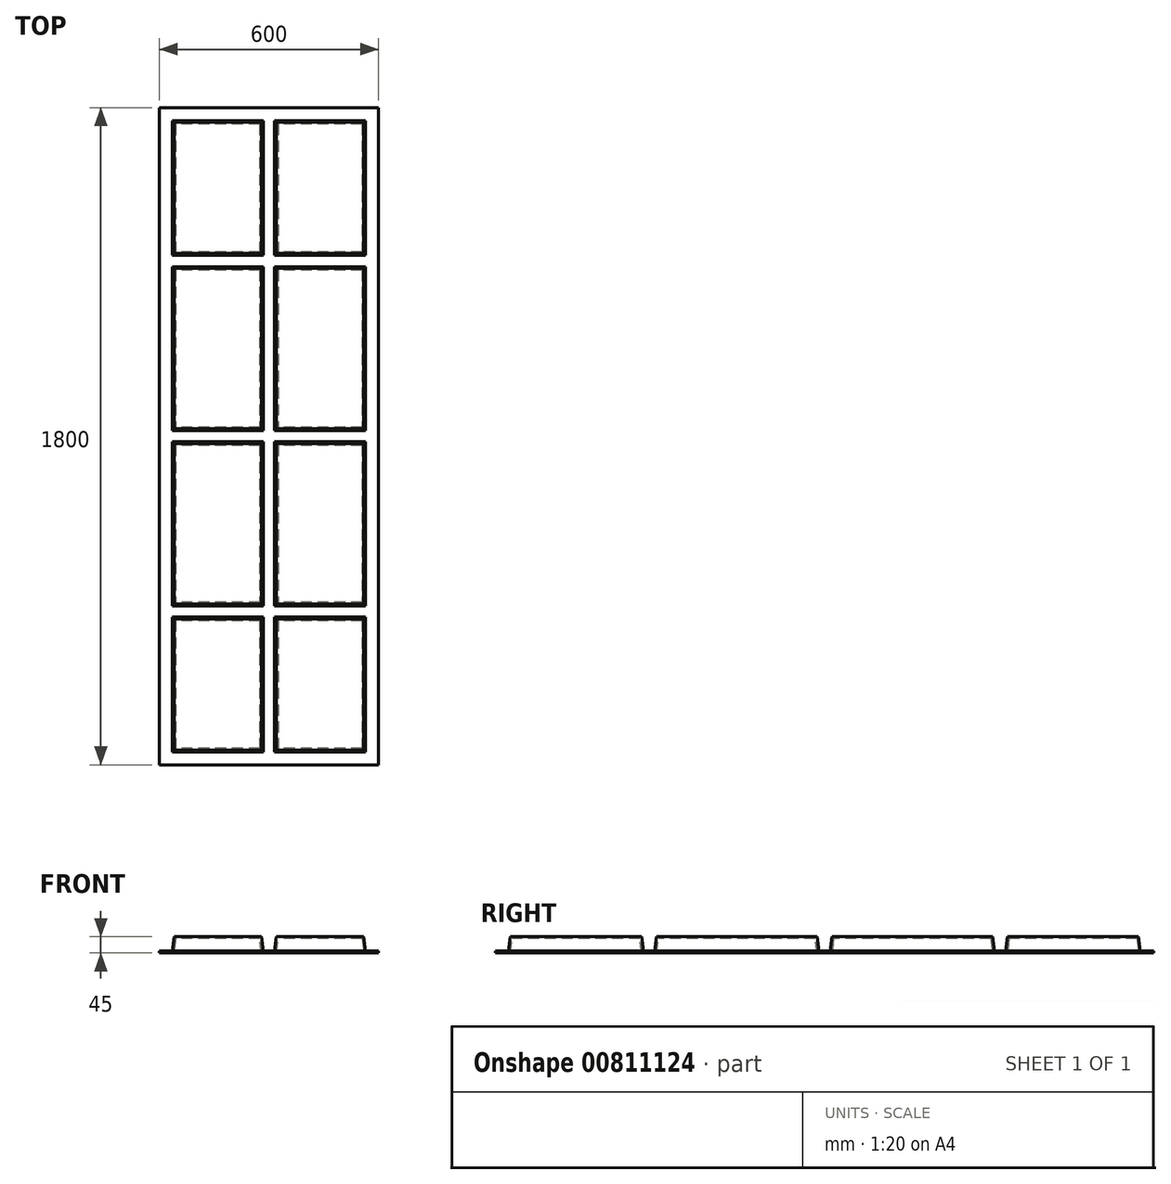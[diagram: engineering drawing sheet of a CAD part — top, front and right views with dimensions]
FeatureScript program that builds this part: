
annotation { "Feature Type Name" : "Feature", "Feature Type Description" : "" }
export const myFeature = defineFeature(function(context is Context, id is Id, definition is map)
    precondition{}
    {
        {
            var Q0;
            Q0=qCreatedBy(makeId("Front.planeOp"),FACE);
            var sketch = newSketch(context, id + "F0", { "sketchPlane" : qUnion([Q0])});
            skLineSegment(sketch, "E0", {"start": v(-170.34, 259.45) * mm, "end": v(-170.34, 254.45) * mm});
            skLineSegment(sketch, "E1.0", {"start": v(129.66, 259.45) * mm, "end": v(129.66, 254.45) * mm});
            skLineSegment(sketch, "E2", {"start": v(-170.34, 254.45) * mm, "end": v(-130.34, 254.45) * mm});
            skLineSegment(sketch, "E3", {"start": v(-125.34, 294.45) * mm, "end": v(104.66, 294.45) * mm});
            skLineSegment(sketch, "E4", {"start": v(109.66, 254.45) * mm, "end": v(129.66, 254.45) * mm});
            skLineSegment(sketch, "E5", {"start": v(-130.34, 254.45) * mm, "end": v(-125.34, 294.45) * mm});
            skLineSegment(sketch, "E6", {"start": v(104.66, 294.45) * mm, "end": v(109.66, 254.45) * mm});
            skLineSegment(sketch, "E7.1", {"start": v(-170.34, 259.45) * mm, "end": v(-134.75, 259.45) * mm});
            skLineSegment(sketch, "E8.1", {"start": v(-134.75, 259.45) * mm, "end": v(-129.75, 299.45) * mm});
            skLineSegment(sketch, "E9.0", {"start": v(114.08, 259.45) * mm, "end": v(129.66, 259.45) * mm});
            skLineSegment(sketch, "E9.1", {"start": v(109.08, 299.45) * mm, "end": v(114.08, 259.45) * mm});
            skLineSegment(sketch, "E9.2", {"start": v(-129.75, 299.45) * mm, "end": v(109.08, 299.45) * mm});
            skLineSegment(sketch, "E10.MirrorCS", {"start": v(149.66, 254.45) * mm, "end": v(129.66, 254.45) * mm});
            skLineSegment(sketch, "E11.MirrorCS", {"start": v(145.25, 259.45) * mm, "end": v(129.66, 259.45) * mm});
            skLineSegment(sketch, "E12.MirrorCS", {"start": v(150.25, 299.45) * mm, "end": v(145.25, 259.45) * mm});
            skLineSegment(sketch, "E13.MirrorCS", {"start": v(154.66, 294.45) * mm, "end": v(149.66, 254.45) * mm});
            skLineSegment(sketch, "E14.MirrorCS", {"start": v(389.08, 299.45) * mm, "end": v(150.25, 299.45) * mm});
            skLineSegment(sketch, "E15.MirrorCS", {"start": v(384.66, 294.45) * mm, "end": v(154.66, 294.45) * mm});
            skLineSegment(sketch, "E16.MirrorCS", {"start": v(394.08, 259.45) * mm, "end": v(389.08, 299.45) * mm});
            skLineSegment(sketch, "E17.MirrorCS", {"start": v(389.66, 254.45) * mm, "end": v(384.66, 294.45) * mm});
            skLineSegment(sketch, "E18.MirrorCS", {"start": v(429.66, 254.45) * mm, "end": v(389.66, 254.45) * mm});
            skLineSegment(sketch, "E19.MirrorCS", {"start": v(429.66, 259.45) * mm, "end": v(429.66, 254.45) * mm});
            skLineSegment(sketch, "E20.MirrorCS", {"start": v(429.66, 259.45) * mm, "end": v(394.08, 259.45) * mm});
            skLineSegment(sketch, "E21", {"start": v(-170.34, 254.45) * mm, "end": v(-170.34, 299.45) * mm});
            skLineSegment(sketch, "E22", {"start": v(-170.34, 299.45) * mm, "end": v(-129.75, 299.45) * mm});
            skLineSegment(sketch, "E23", {"start": v(114.08, 259.45) * mm, "end": v(145.25, 259.45) * mm});
            skLineSegment(sketch, "E24", {"start": v(109.08, 299.45) * mm, "end": v(150.25, 299.45) * mm});
            skLineSegment(sketch, "E25", {"start": v(389.08, 299.45) * mm, "end": v(429.66, 299.45) * mm});
            skLineSegment(sketch, "E26", {"start": v(429.66, 299.45) * mm, "end": v(429.66, 259.45) * mm});
            skSolve(sketch);
        }
        {
            var Q0;
            Q0 = qSketchRegion(id + "F0", true);
            extrude(context, id + "F1", {"entities" : qUnion([Q0]), "oppositeDirection" : true, "depth" : 1800 * mm, "offsetDistance" : 25 * mm});
        }
        {
            var Q0;
            Q0=makeQuery(id+"F1.opExtrude","SWEPT_FACE",FACE,{"disambiguationData":[OSD([sQuery(id+"F0.wireOp",EDGE,"E21")])]});
            var sketch = newSketch(context, id + "F2", { "sketchPlane" : qUnion([Q0])});
            skLineSegment(sketch, "E27", {"start": v(0, 254.45) * mm, "end": v(0, 299.45) * mm});
            skLineSegment(sketch, "E28.0", {"start": v(-900, 254.45) * mm, "end": v(-900, 299.45) * mm});
            skLineSegment(sketch, "E29", {"start": v(-900, 299.45) * mm, "end": v(0, 299.45) * mm});
            skLineSegment(sketch, "E30.0", {"start": v(-880.04, 294.45) * mm, "end": v(-439.96, 294.45) * mm});
            skLineSegment(sketch, "E31", {"start": v(-900, 254.45) * mm, "end": v(0, 254.45) * mm});
            skLineSegment(sketch, "E32.0", {"start": v(-900, 259.45) * mm, "end": v(-884.41, 259.45) * mm});
            skLineSegment(sketch, "E33", {"start": v(-40, 254.45) * mm, "end": v(-45, 294.45) * mm});
            skLineSegment(sketch, "E34", {"start": v(-400, 254.45) * mm, "end": v(-395, 294.45) * mm});
            skLineSegment(sketch, "E35", {"start": v(-440, 254.45) * mm, "end": v(-445, 294.45) * mm});
            skLineSegment(sketch, "E36", {"start": v(-880, 254.45) * mm, "end": v(-875, 294.45) * mm});
            skLineSegment(sketch, "E37.0", {"start": v(-884.41, 259.45) * mm, "end": v(-879.41, 299.45) * mm});
            skLineSegment(sketch, "E38.trimOffspring", {"start": v(-879.37, 259.45) * mm, "end": v(-440.62, 259.45) * mm});
            skLineSegment(sketch, "E39.0", {"start": v(-404.41, 259.45) * mm, "end": v(-399.41, 299.45) * mm});
            skLineSegment(sketch, "E40.0", {"start": v(-435.59, 259.45) * mm, "end": v(-440.59, 299.45) * mm});
            skLineSegment(sketch, "E41.trimOffspring", {"start": v(-400.04, 294.45) * mm, "end": v(-39.96, 294.45) * mm});
            skLineSegment(sketch, "E42.0", {"start": v(-35.59, 259.45) * mm, "end": v(-40.59, 299.45) * mm});
            skLineSegment(sketch, "E43.trimOffspring", {"start": v(-35.59, 259.45) * mm, "end": v(0, 259.45) * mm});
            skLineSegment(sketch, "E44.trimOffspring", {"start": v(-399.38, 259.45) * mm, "end": v(-40.63, 259.45) * mm});
            skLineSegment(sketch, "E45.trimOffspring", {"start": v(-435.59, 259.45) * mm, "end": v(-404.41, 259.45) * mm});
            skLineSegment(sketch, "E46.MirrorCS", {"start": v(-900, 259.45) * mm, "end": v(-915.59, 259.45) * mm});
            skLineSegment(sketch, "E47.MirrorCS", {"start": v(-900, 254.45) * mm, "end": v(-1800, 254.45) * mm});
            skLineSegment(sketch, "E48.MirrorCS", {"start": v(-915.59, 259.45) * mm, "end": v(-920.59, 299.45) * mm});
            skLineSegment(sketch, "E49.MirrorCS", {"start": v(-920, 254.45) * mm, "end": v(-925, 294.45) * mm});
            skLineSegment(sketch, "E50.MirrorCS", {"start": v(-919.96, 294.45) * mm, "end": v(-1360.04, 294.45) * mm});
            skLineSegment(sketch, "E51.MirrorCS", {"start": v(-900, 299.45) * mm, "end": v(-1800, 299.45) * mm});
            skLineSegment(sketch, "E52.MirrorCS", {"start": v(-1364.41, 259.45) * mm, "end": v(-1395.59, 259.45) * mm});
            skLineSegment(sketch, "E53.MirrorCS", {"start": v(-1364.41, 259.45) * mm, "end": v(-1359.41, 299.45) * mm});
            skLineSegment(sketch, "E54.MirrorCS", {"start": v(-1395.59, 259.45) * mm, "end": v(-1400.59, 299.45) * mm});
            skLineSegment(sketch, "E55.MirrorCS", {"start": v(-1360, 254.45) * mm, "end": v(-1355, 294.45) * mm});
            skLineSegment(sketch, "E56.MirrorCS", {"start": v(-1400, 254.45) * mm, "end": v(-1405, 294.45) * mm});
            skLineSegment(sketch, "E57.MirrorCS", {"start": v(-1399.96, 294.45) * mm, "end": v(-1760.04, 294.45) * mm});
            skLineSegment(sketch, "E58.MirrorCS", {"start": v(-1400.63, 259.45) * mm, "end": v(-1759.38, 259.45) * mm});
            skLineSegment(sketch, "E59.MirrorCS", {"start": v(-1764.41, 259.45) * mm, "end": v(-1759.41, 299.45) * mm});
            skLineSegment(sketch, "E60.MirrorCS", {"start": v(-1760, 254.45) * mm, "end": v(-1755, 294.45) * mm});
            skLineSegment(sketch, "E61.MirrorCS", {"start": v(-1764.41, 259.45) * mm, "end": v(-1800, 259.45) * mm});
            skLineSegment(sketch, "E62.MirrorCS", {"start": v(-1800, 254.45) * mm, "end": v(-1800, 299.45) * mm});
            skSolve(sketch);
        }
        {
            var Q0;
            {var subQ0=sQuery(id+"F2.wireOp",EDGE,"E61.MirrorCS");Q0=makeQuery(id+"F2.imprint","IMPRINT",FACE,{"disambiguationData":[TD([[makeQuery(id+"F2.imprint","IMPRINT",EDGE,{"derivedFrom":subQ0}),1.0]])]});}
            extrude(context, id + "F3", {"entities" : qUnion([Q0]), "operationType" : NewBodyOperationType.REMOVE, "oppositeDirection" : true, "depth" : 800 * mm, "offsetDistance" : 25 * mm});
        }
        {
            var Q0;
            {var subQ0=sQuery(id+"F2.wireOp",EDGE,"E61.MirrorCS");Q0=makeQuery(id+"F2.imprint","IMPRINT",FACE,{"disambiguationData":[TD([[makeQuery(id+"F2.imprint","IMPRINT",EDGE,{"derivedFrom":subQ0}),-1.0]])]});}
            extrude(context, id + "F4", {"entities" : qUnion([Q0]), "operationType" : NewBodyOperationType.ADD, "oppositeDirection" : true, "depth" : 600 * mm, "offsetDistance" : 25 * mm});
        }
        {
            var Q0;
            {var subQ0=sQuery(id+"F2.wireOp",EDGE,"E59.MirrorCS");var subQ1=sQuery(id+"F2.wireOp",EDGE,"E57.MirrorCS");var subQ2=makeQuery(id+"F2.imprint","INTERSECT",VERTEX,{"derivedFrom":[subQ1,subQ0]});Q0=makeQuery(id+"F2.imprint","IMPRINT",FACE,{"disambiguationData":[TD([[makeQuery(id+"F2.imprint","IMPRINT",EDGE,{"disambiguationData":[TD([[subQ2,1.0]])],"derivedFrom":subQ1}),1.0]])]});}
            extrude(context, id + "F5", {"entities" : qUnion([Q0]), "operationType" : NewBodyOperationType.ADD, "oppositeDirection" : true, "depth" : 600 * mm, "offsetDistance" : 25 * mm});
        }
        {
            var Q0;
            {var subQ1=sQuery(id+"F2.wireOp",EDGE,"E52.MirrorCS");Q0=makeQuery(id+"F2.imprint","IMPRINT",FACE,{"disambiguationData":[TD([[makeQuery(id+"F2.imprint","IMPRINT",EDGE,{"derivedFrom":subQ1}),1.0]])]});}
            var Q1;
            {var subQ2=sQuery(id+"F2.wireOp",EDGE,"E32.0");Q1=makeQuery(id+"F2.imprint","IMPRINT",FACE,{"disambiguationData":[TD([[makeQuery(id+"F2.imprint","IMPRINT",EDGE,{"derivedFrom":subQ2}),1.0]])]});}
            var Q2;
            {var subQ1=sQuery(id+"F2.wireOp",EDGE,"E46.MirrorCS");Q2=makeQuery(id+"F2.imprint","IMPRINT",FACE,{"disambiguationData":[TD([[makeQuery(id+"F2.imprint","IMPRINT",EDGE,{"derivedFrom":subQ1}),1.0]])]});}
            var Q3;
            {var subQ4=sQuery(id+"F2.wireOp",EDGE,"E45.trimOffspring");Q3=makeQuery(id+"F2.imprint","IMPRINT",FACE,{"disambiguationData":[TD([[makeQuery(id+"F2.imprint","IMPRINT",EDGE,{"derivedFrom":subQ4}),1.0]])]});}
            var Q4;
            {var subQ6=sQuery(id+"F2.wireOp",EDGE,"E43.trimOffspring");Q4=makeQuery(id+"F2.imprint","IMPRINT",FACE,{"disambiguationData":[TD([[makeQuery(id+"F2.imprint","IMPRINT",EDGE,{"derivedFrom":subQ6}),1.0]])]});}
            extrude(context, id + "F6", {"entities" : qUnion([Q0, Q1, Q2, Q3, Q4]), "operationType" : NewBodyOperationType.REMOVE, "oppositeDirection" : true, "depth" : 800 * mm, "offsetDistance" : 25 * mm});
        }
        {
            var Q0;
            {var subQ0=sQuery(id+"F2.wireOp",EDGE,"E41.trimOffspring");var subQ1=sQuery(id+"F2.wireOp",EDGE,"E33");var subQ2=makeQuery(id+"F2.imprint","INTERSECT",VERTEX,{"derivedFrom":[subQ1,subQ0]});Q0=makeQuery(id+"F2.imprint","IMPRINT",FACE,{"disambiguationData":[TD([[makeQuery(id+"F2.imprint","IMPRINT",EDGE,{"disambiguationData":[TD([[subQ2,-1.0]])],"derivedFrom":subQ0}),-1.0]])]});}
            var Q1;
            {var subQ0=sQuery(id+"F2.wireOp",EDGE,"E43.trimOffspring");Q1=makeQuery(id+"F2.imprint","IMPRINT",FACE,{"disambiguationData":[TD([[makeQuery(id+"F2.imprint","IMPRINT",EDGE,{"derivedFrom":subQ0}),-1.0]])]});}
            var Q2;
            {var subQ0=sQuery(id+"F2.wireOp",EDGE,"E40.0");var subQ1=sQuery(id+"F2.wireOp",EDGE,"E30.0");var subQ2=makeQuery(id+"F2.imprint","INTERSECT",VERTEX,{"derivedFrom":[subQ1,subQ0]});Q2=makeQuery(id+"F2.imprint","IMPRINT",FACE,{"disambiguationData":[TD([[makeQuery(id+"F2.imprint","IMPRINT",EDGE,{"disambiguationData":[TD([[subQ2,1.0]])],"derivedFrom":subQ1}),-1.0]])]});}
            var Q3;
            {var subQ5=sQuery(id+"F2.wireOp",EDGE,"E45.trimOffspring");Q3=makeQuery(id+"F2.imprint","IMPRINT",FACE,{"disambiguationData":[TD([[makeQuery(id+"F2.imprint","IMPRINT",EDGE,{"derivedFrom":subQ5}),-1.0]])]});}
            var Q4;
            {var subQ0=sQuery(id+"F2.wireOp",EDGE,"E41.trimOffspring");var subQ1=sQuery(id+"F2.wireOp",EDGE,"E34");var subQ2=makeQuery(id+"F2.imprint","INTERSECT",VERTEX,{"derivedFrom":[subQ1,subQ0]});Q4=makeQuery(id+"F2.imprint","IMPRINT",FACE,{"disambiguationData":[TD([[makeQuery(id+"F2.imprint","IMPRINT",EDGE,{"disambiguationData":[TD([[subQ2,1.0]])],"derivedFrom":subQ0}),-1.0]])]});}
            var Q5;
            {var subQ3=sQuery(id+"F2.wireOp",EDGE,"E50.MirrorCS");var subQ5=sQuery(id+"F2.wireOp",EDGE,"E49.MirrorCS");var subQ6=makeQuery(id+"F2.imprint","INTERSECT",VERTEX,{"derivedFrom":[subQ5,subQ3]});Q5=makeQuery(id+"F2.imprint","IMPRINT",FACE,{"disambiguationData":[TD([[makeQuery(id+"F2.imprint","IMPRINT",EDGE,{"disambiguationData":[TD([[subQ6,1.0]])],"derivedFrom":subQ3}),1.0]])]});}
            var Q6;
            {var subQ7=sQuery(id+"F2.wireOp",EDGE,"E46.MirrorCS");Q6=makeQuery(id+"F2.imprint","IMPRINT",FACE,{"disambiguationData":[TD([[makeQuery(id+"F2.imprint","IMPRINT",EDGE,{"derivedFrom":subQ7}),-1.0]])]});}
            var Q7;
            {var subQ7=sQuery(id+"F2.wireOp",EDGE,"E32.0");Q7=makeQuery(id+"F2.imprint","IMPRINT",FACE,{"disambiguationData":[TD([[makeQuery(id+"F2.imprint","IMPRINT",EDGE,{"derivedFrom":subQ7}),-1.0]])]});}
            var Q8;
            {var subQ0=sQuery(id+"F2.wireOp",EDGE,"E37.0");var subQ1=sQuery(id+"F2.wireOp",EDGE,"E30.0");var subQ2=makeQuery(id+"F2.imprint","INTERSECT",VERTEX,{"derivedFrom":[subQ1,subQ0]});Q8=makeQuery(id+"F2.imprint","IMPRINT",FACE,{"disambiguationData":[TD([[makeQuery(id+"F2.imprint","IMPRINT",EDGE,{"disambiguationData":[TD([[subQ2,-1.0]])],"derivedFrom":subQ1}),-1.0]])]});}
            var Q9;
            {var subQ3=sQuery(id+"F2.wireOp",EDGE,"E57.MirrorCS");var subQ5=sQuery(id+"F2.wireOp",EDGE,"E56.MirrorCS");var subQ6=makeQuery(id+"F2.imprint","INTERSECT",VERTEX,{"derivedFrom":[subQ5,subQ3]});Q9=makeQuery(id+"F2.imprint","IMPRINT",FACE,{"disambiguationData":[TD([[makeQuery(id+"F2.imprint","IMPRINT",EDGE,{"disambiguationData":[TD([[subQ6,1.0]])],"derivedFrom":subQ3}),1.0]])]});}
            var Q10;
            {var subQ5=sQuery(id+"F2.wireOp",EDGE,"E52.MirrorCS");Q10=makeQuery(id+"F2.imprint","IMPRINT",FACE,{"disambiguationData":[TD([[makeQuery(id+"F2.imprint","IMPRINT",EDGE,{"derivedFrom":subQ5}),-1.0]])]});}
            var Q11;
            {var subQ0=sQuery(id+"F2.wireOp",EDGE,"E53.MirrorCS");var subQ1=sQuery(id+"F2.wireOp",EDGE,"E50.MirrorCS");var subQ2=makeQuery(id+"F2.imprint","INTERSECT",VERTEX,{"derivedFrom":[subQ1,subQ0]});Q11=makeQuery(id+"F2.imprint","IMPRINT",FACE,{"disambiguationData":[TD([[makeQuery(id+"F2.imprint","IMPRINT",EDGE,{"disambiguationData":[TD([[subQ2,1.0]])],"derivedFrom":subQ1}),1.0]])]});}
            extrude(context, id + "F7", {"entities" : qUnion([Q0, Q1, Q2, Q3, Q4, Q5, Q6, Q7, Q8, Q9, Q10, Q11]), "operationType" : NewBodyOperationType.ADD, "oppositeDirection" : true, "depth" : 600 * mm, "offsetDistance" : 25 * mm});
        }
        {
            var Q0;
            {var subQ0=sQuery(id+"F0.wireOp",EDGE,"E7.1");Q0=makeQuery(id+"F0.imprint","IMPRINT",FACE,{"disambiguationData":[TD([[makeQuery(id+"F0.imprint","IMPRINT",EDGE,{"derivedFrom":subQ0}),1.0]])]});}
            extrude(context, id + "F8", {"entities" : qUnion([Q0]), "operationType" : NewBodyOperationType.REMOVE, "oppositeDirection" : true, "depth" : 1900 * mm, "offsetDistance" : 25 * mm});
        }
        {
            var Q0;
            {var subQ3=sQuery(id+"F0.wireOp",EDGE,"E9.1");Q0=makeQuery(id+"F0.imprint","IMPRINT",FACE,{"disambiguationData":[TD([[makeQuery(id+"F0.imprint","IMPRINT",EDGE,{"derivedFrom":subQ3}),1.0]])]});}
            extrude(context, id + "F9", {"entities" : qUnion([Q0]), "operationType" : NewBodyOperationType.REMOVE, "oppositeDirection" : true, "depth" : 1900 * mm, "offsetDistance" : 25 * mm});
        }
        {
            var Q0;
            Q0=makeQuery(id+"F0.imprint","IMPRINT",FACE,{"disambiguationData":[TD([[makeQuery(id+"F0.imprint","IMPRINT",EDGE,{"derivedFrom":sQuery(id+"F0.wireOp",EDGE,"E16.MirrorCS")}),-1.0]])]});
            extrude(context, id + "F10", {"entities" : qUnion([Q0]), "operationType" : NewBodyOperationType.REMOVE, "oppositeDirection" : true, "depth" : 1900 * mm, "offsetDistance" : 25 * mm});
        }
        {
            var Q0;
            {var subQ4=sQuery(id+"F2.wireOp",EDGE,"E61.MirrorCS");Q0=makeQuery(id+"F2.imprint","IMPRINT",FACE,{"disambiguationData":[TD([[makeQuery(id+"F2.imprint","IMPRINT",EDGE,{"derivedFrom":subQ4}),-1.0]])]});}
            var Q1;
            {var subQ1=sQuery(id+"F2.wireOp",EDGE,"E52.MirrorCS");Q1=makeQuery(id+"F2.imprint","IMPRINT",FACE,{"disambiguationData":[TD([[makeQuery(id+"F2.imprint","IMPRINT",EDGE,{"derivedFrom":subQ1}),-1.0]])]});}
            var Q2;
            {var subQ1=sQuery(id+"F2.wireOp",EDGE,"E46.MirrorCS");Q2=makeQuery(id+"F2.imprint","IMPRINT",FACE,{"disambiguationData":[TD([[makeQuery(id+"F2.imprint","IMPRINT",EDGE,{"derivedFrom":subQ1}),-1.0]])]});}
            extrude(context, id + "F11", {"entities" : qUnion([Q0, Q1, Q2]), "operationType" : NewBodyOperationType.REMOVE, "oppositeDirection" : true, "depth" : 800 * mm, "offsetDistance" : 25 * mm});
        }
    });
